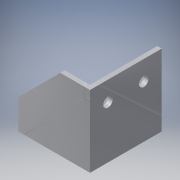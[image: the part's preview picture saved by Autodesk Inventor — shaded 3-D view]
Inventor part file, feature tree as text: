
AUTODESK INVENTOR PART (.ipt)
format: ipt  version: 2016 (Build 200138000, 138)  size: 110,592 bytes
history: native  units: in
note: dims shown in document units (in); Inventor stores cm internally (conversion verified against a paired STEP export)
features: sketch x4, other x3
ambient origin geometry x8: Origin, YZ Plane, XZ Plane, XY Plane, X Axis, Y Axis, Z Axis, Center Point
bodies: Solid1 (feature_tree)
feature tree (7):
  other  "top left rail gusset.ipt"
  other  "Solid1::top left rail gusset.ipt"
  other  "TaggingFeature1"
  sketch  "Sketch1"  dims[d0=0.3937in]
  sketch  "Sketch2"
  sketch  "Sketch3"
  sketch  "Sketch5"
